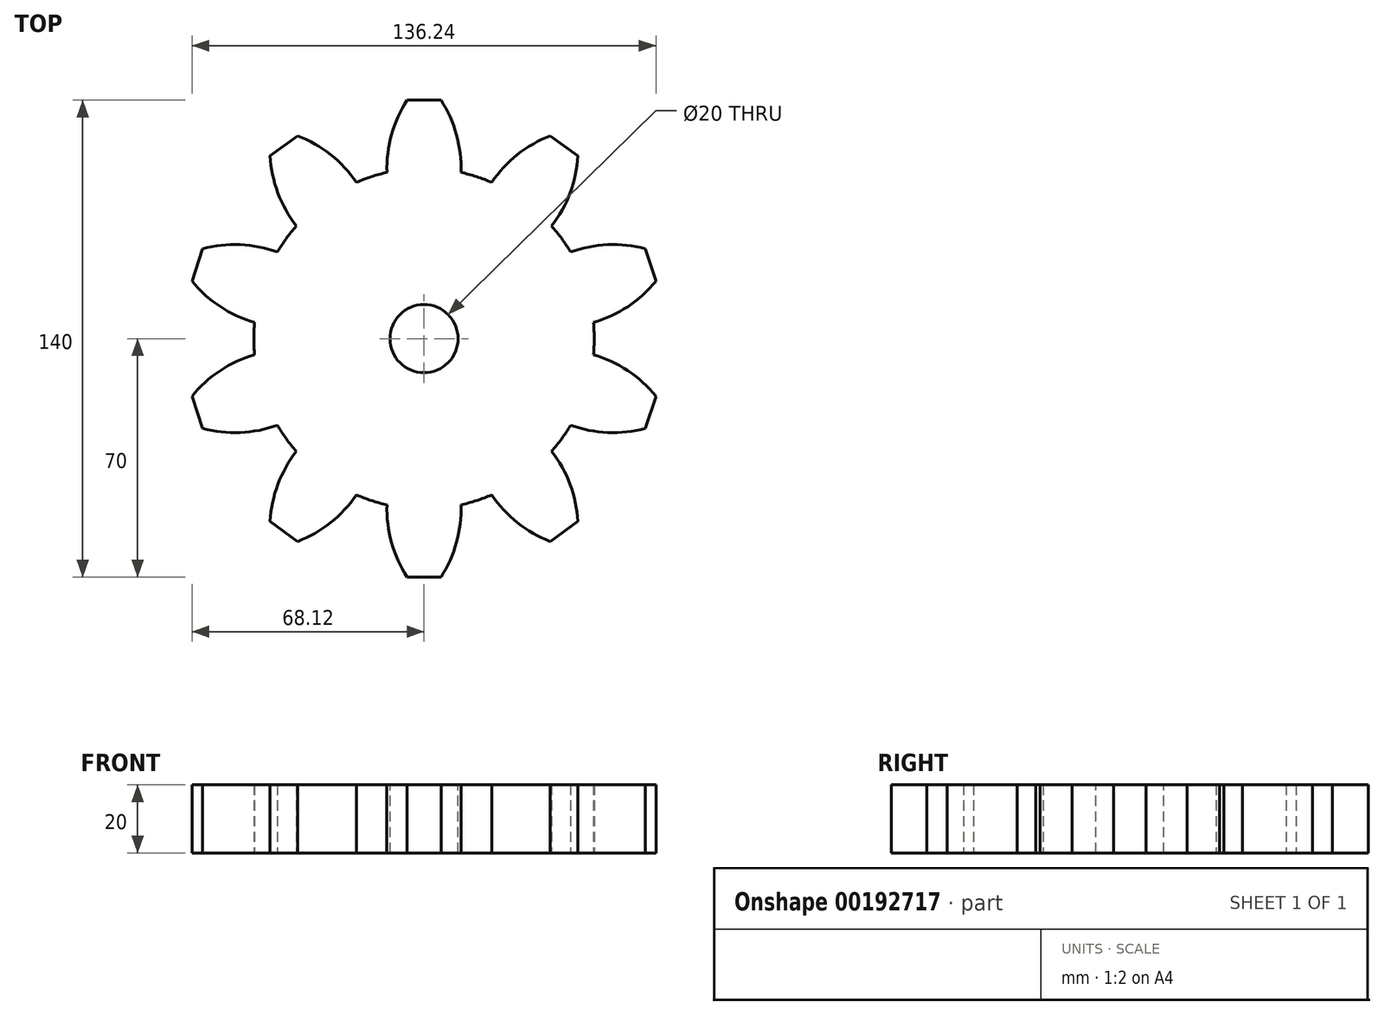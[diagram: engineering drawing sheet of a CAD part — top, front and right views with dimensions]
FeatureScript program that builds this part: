
annotation { "Feature Type Name" : "Feature", "Feature Type Description" : "" }
export const myFeature = defineFeature(function(context is Context, id is Id, definition is map)
    precondition{}
    {
        {
            var Q0;
            Q0=qCreatedBy(makeId("Top.planeOp"),FACE);
            var sketch = newSketch(context, id + "F0", { "sketchPlane" : qUnion([Q0])});
            skCircle(sketch, "E0", {"center": v(0, 0) * mm, "radius": 50 * mm});
            skLineSegment(sketch, "E1", {"start": v(0, 0) * mm, "end": v(0, 50) * mm, "construction": true});
            skLineSegment(sketch, "E2", {"start": v(0, 50) * mm, "end": v(0, 70) * mm});
            skLineSegment(sketch, "E3", {"start": v(0, 70) * mm, "end": v(-5, 70) * mm});
            skArc(sketch, "E4", {"start": v(-5, 70) * mm, "mid": v(-9.55, 59.85) * mm, "end": v(-10.87, 48.8) * mm});
            skLineSegment(sketch, "E5.MirrorCS", {"start": v(0, 70) * mm, "end": v(5, 70) * mm});
            skArc(sketch, "E6.MirrorCS", {"start": v(5, 70) * mm, "mid": v(9.55, 59.85) * mm, "end": v(10.87, 48.8) * mm});
            skArc(sketch, "E7.1.0", {"start": v(-45.2, 53.7) * mm, "mid": v(-42.9, 42.8) * mm, "end": v(-37.48, 33.1) * mm});
            skLineSegment(sketch, "E7.1.1", {"start": v(-41.14, 56.63) * mm, "end": v(-45.2, 53.7) * mm});
            skLineSegment(sketch, "E7.1.2", {"start": v(-41.14, 56.63) * mm, "end": v(-37.1, 59.57) * mm});
            skArc(sketch, "E7.1.3", {"start": v(-37.1, 59.57) * mm, "mid": v(-27.45, 54.03) * mm, "end": v(-19.9, 45.87) * mm});
            skArc(sketch, "E7.2.0", {"start": v(-68.12, 16.88) * mm, "mid": v(-59.87, 9.4) * mm, "end": v(-49.77, 4.74) * mm});
            skLineSegment(sketch, "E7.2.1", {"start": v(-66.57, 21.63) * mm, "end": v(-68.12, 16.88) * mm});
            skLineSegment(sketch, "E7.2.2", {"start": v(-66.57, 21.63) * mm, "end": v(-65.03, 26.39) * mm});
            skArc(sketch, "E7.2.3", {"start": v(-65.03, 26.39) * mm, "mid": v(-53.97, 27.58) * mm, "end": v(-43.06, 25.42) * mm});
            skArc(sketch, "E7.3.0", {"start": v(-65.03, -26.39) * mm, "mid": v(-53.97, -27.58) * mm, "end": v(-43.06, -25.42) * mm});
            skLineSegment(sketch, "E7.3.1", {"start": v(-66.57, -21.63) * mm, "end": v(-65.03, -26.39) * mm});
            skLineSegment(sketch, "E7.3.2", {"start": v(-66.57, -21.63) * mm, "end": v(-68.12, -16.88) * mm});
            skArc(sketch, "E7.3.3", {"start": v(-68.12, -16.88) * mm, "mid": v(-59.87, -9.4) * mm, "end": v(-49.77, -4.74) * mm});
            skArc(sketch, "E7.4.0", {"start": v(-37.1, -59.57) * mm, "mid": v(-27.45, -54.03) * mm, "end": v(-19.9, -45.87) * mm});
            skLineSegment(sketch, "E7.4.1", {"start": v(-41.14, -56.63) * mm, "end": v(-37.1, -59.57) * mm});
            skLineSegment(sketch, "E7.4.2", {"start": v(-41.14, -56.63) * mm, "end": v(-45.2, -53.7) * mm});
            skArc(sketch, "E7.4.3", {"start": v(-45.2, -53.7) * mm, "mid": v(-42.9, -42.8) * mm, "end": v(-37.48, -33.1) * mm});
            skArc(sketch, "E7.5.0", {"start": v(5, -70) * mm, "mid": v(9.55, -59.85) * mm, "end": v(10.87, -48.8) * mm});
            skLineSegment(sketch, "E7.5.1", {"start": v(0, -70) * mm, "end": v(5, -70) * mm});
            skLineSegment(sketch, "E7.5.2", {"start": v(0, -70) * mm, "end": v(-5, -70) * mm});
            skArc(sketch, "E7.5.3", {"start": v(-5, -70) * mm, "mid": v(-9.55, -59.85) * mm, "end": v(-10.87, -48.8) * mm});
            skArc(sketch, "E7.6.0", {"start": v(45.2, -53.7) * mm, "mid": v(42.9, -42.8) * mm, "end": v(37.48, -33.1) * mm});
            skLineSegment(sketch, "E7.6.1", {"start": v(41.14, -56.63) * mm, "end": v(45.2, -53.7) * mm});
            skLineSegment(sketch, "E7.6.2", {"start": v(41.14, -56.63) * mm, "end": v(37.1, -59.57) * mm});
            skArc(sketch, "E7.6.3", {"start": v(37.1, -59.57) * mm, "mid": v(27.45, -54.03) * mm, "end": v(19.9, -45.87) * mm});
            skArc(sketch, "E7.7.0", {"start": v(68.12, -16.88) * mm, "mid": v(59.87, -9.4) * mm, "end": v(49.77, -4.74) * mm});
            skLineSegment(sketch, "E7.7.1", {"start": v(66.57, -21.63) * mm, "end": v(68.12, -16.88) * mm});
            skLineSegment(sketch, "E7.7.2", {"start": v(66.57, -21.63) * mm, "end": v(65.03, -26.39) * mm});
            skArc(sketch, "E7.7.3", {"start": v(65.03, -26.39) * mm, "mid": v(53.97, -27.58) * mm, "end": v(43.06, -25.42) * mm});
            skArc(sketch, "E7.8.0", {"start": v(65.03, 26.39) * mm, "mid": v(53.97, 27.58) * mm, "end": v(43.06, 25.42) * mm});
            skLineSegment(sketch, "E7.8.1", {"start": v(66.57, 21.63) * mm, "end": v(65.03, 26.39) * mm});
            skLineSegment(sketch, "E7.8.2", {"start": v(66.57, 21.63) * mm, "end": v(68.12, 16.88) * mm});
            skArc(sketch, "E7.8.3", {"start": v(68.12, 16.88) * mm, "mid": v(59.87, 9.4) * mm, "end": v(49.77, 4.74) * mm});
            skArc(sketch, "E7.9.0", {"start": v(37.1, 59.57) * mm, "mid": v(27.45, 54.03) * mm, "end": v(19.9, 45.87) * mm});
            skLineSegment(sketch, "E7.9.1", {"start": v(41.14, 56.63) * mm, "end": v(37.1, 59.57) * mm});
            skLineSegment(sketch, "E7.9.2", {"start": v(41.14, 56.63) * mm, "end": v(45.2, 53.7) * mm});
            skArc(sketch, "E7.9.3", {"start": v(45.2, 53.7) * mm, "mid": v(42.9, 42.8) * mm, "end": v(37.48, 33.1) * mm});
            skSolve(sketch);
        }
        {
            var Q0;
            Q0=qSketchRegion(id+"F0",true);
            extrude(context, id + "F1", {"entities" : qUnion([Q0]), "depth" : 20 * mm});
        }
        {
            var Q0;
            Q0=makeQuery(id+"F1.opExtrude","CAP_FACE",FACE,{"disambiguationData":[OSD([sQuery(id+"F0.wireOp",EDGE,"E0"),sQuery(id+"F0.wireOp",EDGE,"E3"),sQuery(id+"F0.wireOp",EDGE,"E4"),sQuery(id+"F0.wireOp",EDGE,"E5.MirrorCS"),sQuery(id+"F0.wireOp",EDGE,"E6.MirrorCS"),sQuery(id+"F0.wireOp",EDGE,"E7.1.0"),sQuery(id+"F0.wireOp",EDGE,"E7.1.1"),sQuery(id+"F0.wireOp",EDGE,"E7.1.2"),sQuery(id+"F0.wireOp",EDGE,"E7.1.3"),sQuery(id+"F0.wireOp",EDGE,"E7.2.0"),sQuery(id+"F0.wireOp",EDGE,"E7.2.1"),sQuery(id+"F0.wireOp",EDGE,"E7.2.2"),sQuery(id+"F0.wireOp",EDGE,"E7.2.3"),sQuery(id+"F0.wireOp",EDGE,"E7.3.0"),sQuery(id+"F0.wireOp",EDGE,"E7.3.1"),sQuery(id+"F0.wireOp",EDGE,"E7.3.2"),sQuery(id+"F0.wireOp",EDGE,"E7.3.3"),sQuery(id+"F0.wireOp",EDGE,"E7.4.0"),sQuery(id+"F0.wireOp",EDGE,"E7.4.1"),sQuery(id+"F0.wireOp",EDGE,"E7.4.2"),sQuery(id+"F0.wireOp",EDGE,"E7.4.3"),sQuery(id+"F0.wireOp",EDGE,"E7.5.0"),sQuery(id+"F0.wireOp",EDGE,"E7.5.1"),sQuery(id+"F0.wireOp",EDGE,"E7.5.2"),sQuery(id+"F0.wireOp",EDGE,"E7.5.3"),sQuery(id+"F0.wireOp",EDGE,"E7.6.0"),sQuery(id+"F0.wireOp",EDGE,"E7.6.1"),sQuery(id+"F0.wireOp",EDGE,"E7.6.2"),sQuery(id+"F0.wireOp",EDGE,"E7.6.3"),sQuery(id+"F0.wireOp",EDGE,"E7.7.0"),sQuery(id+"F0.wireOp",EDGE,"E7.7.1"),sQuery(id+"F0.wireOp",EDGE,"E7.7.2"),sQuery(id+"F0.wireOp",EDGE,"E7.7.3"),sQuery(id+"F0.wireOp",EDGE,"E7.8.0"),sQuery(id+"F0.wireOp",EDGE,"E7.8.1"),sQuery(id+"F0.wireOp",EDGE,"E7.8.2"),sQuery(id+"F0.wireOp",EDGE,"E7.8.3"),sQuery(id+"F0.wireOp",EDGE,"E7.9.0"),sQuery(id+"F0.wireOp",EDGE,"E7.9.1"),sQuery(id+"F0.wireOp",EDGE,"E7.9.2"),sQuery(id+"F0.wireOp",EDGE,"E7.9.3"),sQuery(id+"F0.wireOp",EDGE,"E7.10.0"),sQuery(id+"F0.wireOp",EDGE,"E7.10.1"),sQuery(id+"F0.wireOp",EDGE,"E7.10.2"),sQuery(id+"F0.wireOp",EDGE,"E7.10.3"),sQuery(id+"F0.wireOp",EDGE,"E7.11.0"),sQuery(id+"F0.wireOp",EDGE,"E7.11.1"),sQuery(id+"F0.wireOp",EDGE,"E7.11.2"),sQuery(id+"F0.wireOp",EDGE,"E7.11.3"),sQuery(id+"F0.wireOp",EDGE,"E7.12.0"),sQuery(id+"F0.wireOp",EDGE,"E7.12.1"),sQuery(id+"F0.wireOp",EDGE,"E7.12.2"),sQuery(id+"F0.wireOp",EDGE,"E7.12.3"),sQuery(id+"F0.wireOp",EDGE,"E7.13.0"),sQuery(id+"F0.wireOp",EDGE,"E7.13.1"),sQuery(id+"F0.wireOp",EDGE,"E7.13.2"),sQuery(id+"F0.wireOp",EDGE,"E7.13.3"),sQuery(id+"F0.wireOp",EDGE,"E7.14.0"),sQuery(id+"F0.wireOp",EDGE,"E7.14.1"),sQuery(id+"F0.wireOp",EDGE,"E7.14.2"),sQuery(id+"F0.wireOp",EDGE,"E7.14.3"),sQuery(id+"F0.wireOp",EDGE,"E7.15.0"),sQuery(id+"F0.wireOp",EDGE,"E7.15.1"),sQuery(id+"F0.wireOp",EDGE,"E7.15.2"),sQuery(id+"F0.wireOp",EDGE,"E7.15.3")])],"isStart":false});
            var sketch = newSketch(context, id + "F2", { "sketchPlane" : qUnion([Q0])});
            skCircle(sketch, "E8", {"center": v(0, 0) * mm, "radius": 10 * mm});
            skSolve(sketch);
        }
        {
            var Q0;
            Q0 = qSketchRegion(id + "F2", true);
            extrude(context, id + "F3", {"entities" : qUnion([Q0]), "operationType" : NewBodyOperationType.REMOVE, "endBound" : BoundingType.UP_TO_NEXT, "oppositeDirection" : true, "depth" : 25 * mm});
        }
    });
